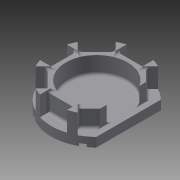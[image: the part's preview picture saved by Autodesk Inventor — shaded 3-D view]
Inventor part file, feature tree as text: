
AUTODESK INVENTOR PART (.ipt)
format: ipt  version: 2015 (Build 190159000, 159)  size: 380,416 bytes
history: native  units: in
note: dims shown in document units (in); Inventor stores cm internally (conversion verified against a paired STEP export)
features: extrude x6, sketch x3, fillet x3, chamfer x1
ambient origin geometry x8: Origin, YZ Plane, XZ Plane, XY Plane, X Axis, Y Axis, Z Axis, Center Point
bodies: Body1 (feature_tree)
feature tree (13):
  sketch  "Sketch7"  dims[d66=0.1181in d67=0.315in]
  sketch  "Sketch8"  dims[d69=135.0deg d70=0.8661in]
  sketch  "Sketch9"  dims[d71=0.0295in d72=0.0295in d73=0.0295in d74=0.0295in d75=0.0295in d76=0.0295in d77=0.0295in d78=0.0295in d79=0.0295in d80=0.0295in d81=0.0295in d82=0.0295in d83=0.0295in d84=0.0295in d85=0.0295in d86=0.0295in d87=0.7874in d97=0.1181in d98=0.0in d99=0.6299in d100=0.0in d101=0.7087in d102=0.0in d111=0.0787in d112=0.0787in d113=0.0787in d114=0.7972in d115=0.7972in d116=1.1909in d117=1.1909in d118=0.1575in d119=0.1181in d120=0.0in d121=0.1575in d122=0.0in d123=0.1575in d124=0.1575in d125=0.1575in d126=0.1575in d127=0.0787in d128=0.0in d129=0.0591in d130=0.0787in d131=45.0deg]
  extrude  "Extrusion9"  Depth=0.315in
  extrude  "Extrusion10"  Depth=0.8661in
  extrude  "Extrusion11"  Depth=0.0787in
  fillet  "Fillet4"  Radius=0.0295in
  fillet  "Fillet5"  Radius=0.0295in
  fillet  "Fillet6"  Radius=0.0295in
  extrude  "Extrusion13"  Depth=0.0787in
  extrude  "Extrusion14"  Depth=0.0787in
  extrude  "Extrusion15"  Depth=0.0787in
  chamfer  "Chamfer6"  Distance=0.0295in
